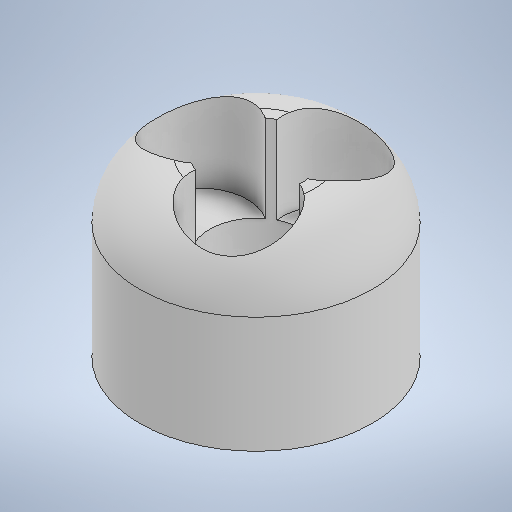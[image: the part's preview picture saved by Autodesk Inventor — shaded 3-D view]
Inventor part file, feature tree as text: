
AUTODESK INVENTOR PART (.ipt)
format: ipt  version: 2025.1 (Build 291241000, 241)  size: 260,096 bytes
history: native  units: in
note: dims shown in document units (in); Inventor stores cm internally (conversion verified against a paired STEP export)
features: extrude x2, sketch x1, fillet x1
ambient origin geometry x8: Origin, YZ Plane, XZ Plane, XY Plane, X Axis, Y Axis, Z Axis, Center Point
bodies: Solid1 (feature_tree)
feature tree (4):
  sketch  "Sketch1"  dims[d3=0.2in d7=0.2in d8=0.5in d9=0.1875in d10=0.0in d11=0.375in d12=0.0in d13=0.125in d14=0.2in d15=0.2in]
  extrude  "Extrusion1"  Depth=0.125in
  extrude  "Extrusion2"  Depth=0.125in
  fillet  "Fillet1"  Radius=0.1875in
